# Revit family: Bath-Drop_In_Whirlpool_Heater-KOHLER-RiverBath-K-1394_11
name_source: partatom
category: Plumbing Fixtures
revit_build: Autodesk Revit 2015 (Build: 20140606_1530(x64)
units: mm (PartAtom-declared; Revit-internal decimal feet)

## types (4) — shared parameters
ADA Compliant = No
Amplifier Electrical Connector = Amplifier Electrical Connector
Apparent Load = 4800 VA
Assembly Code = D2010500
Blower Electrical Connector = Blower Electrical Connector
CW Connection = No
Cold Water Inlet = Cold Water Inlet
Date Modified = 12/07/2018
Default Elevation = 0"
Drain Included = No
Electrical Connector = Yes
Electrical Note = Two dedicated circuits required, protected with Class A Ground-Fault Circuit-Interrupter (GFCI) or Residual Current Device (RCD)
HW Connection = No
Heater Electrical Connector = Heater Electrical Connector
Height = 25"
Hot Water Inlet = Hot Water Inlet
Length = 66"
Manufacturer = KOHLER Co.
MasterFormat 1995 = 15410
MasterFormat 2004 = 22.41.19
Material = Acrylic
Product Documentation Link = http://www.us.kohler.com
Product Name = RiverBath
Product Page URL = http://www.us.kohler.com
Pump Electrical Connector = Pump Electrical Connector
URL = https://www.us.kohler.com
Vent Connection = No
Voltage = 240 V
Waste Connection = Yes
Waste Water Outlet = Waste Water Outlet
Width = 66"

## per-type parameters (varying)
| type | Description | Finish | Model | Type | With chromatherapy |
| With chromatherapy, 0-White | 66 Inch drop-in whirlpool with chromatherapy and heater without jet trim | Kohler-Acrylic-0-White | K-1394-H2-0 | 1 | Yes |
| With chromatherapy, 96-Biscuit | 66 Inch drop-in whirlpool with chromatherapy and heater without jet trim | Kohler-Acrylic-96-Biscuit | K-1394-H2-96 | 2 | Yes |
| Without chromatherapy, 0-White | 66 Inch drop-in whirlpool with heater without jet trim | Kohler-Acrylic-0-White | K-1394-H3-0 | 3 | No |
| Without chromatherapy, 96-Biscuit | 66 Inch drop-in whirlpool with heater without jet trim | Kohler-Acrylic-96-Biscuit | K-1394-H3-96 | 4 | No |

## geometry (parser evidence)
native form markers: Sweep x5
no freeform markers — native parametric forms only
